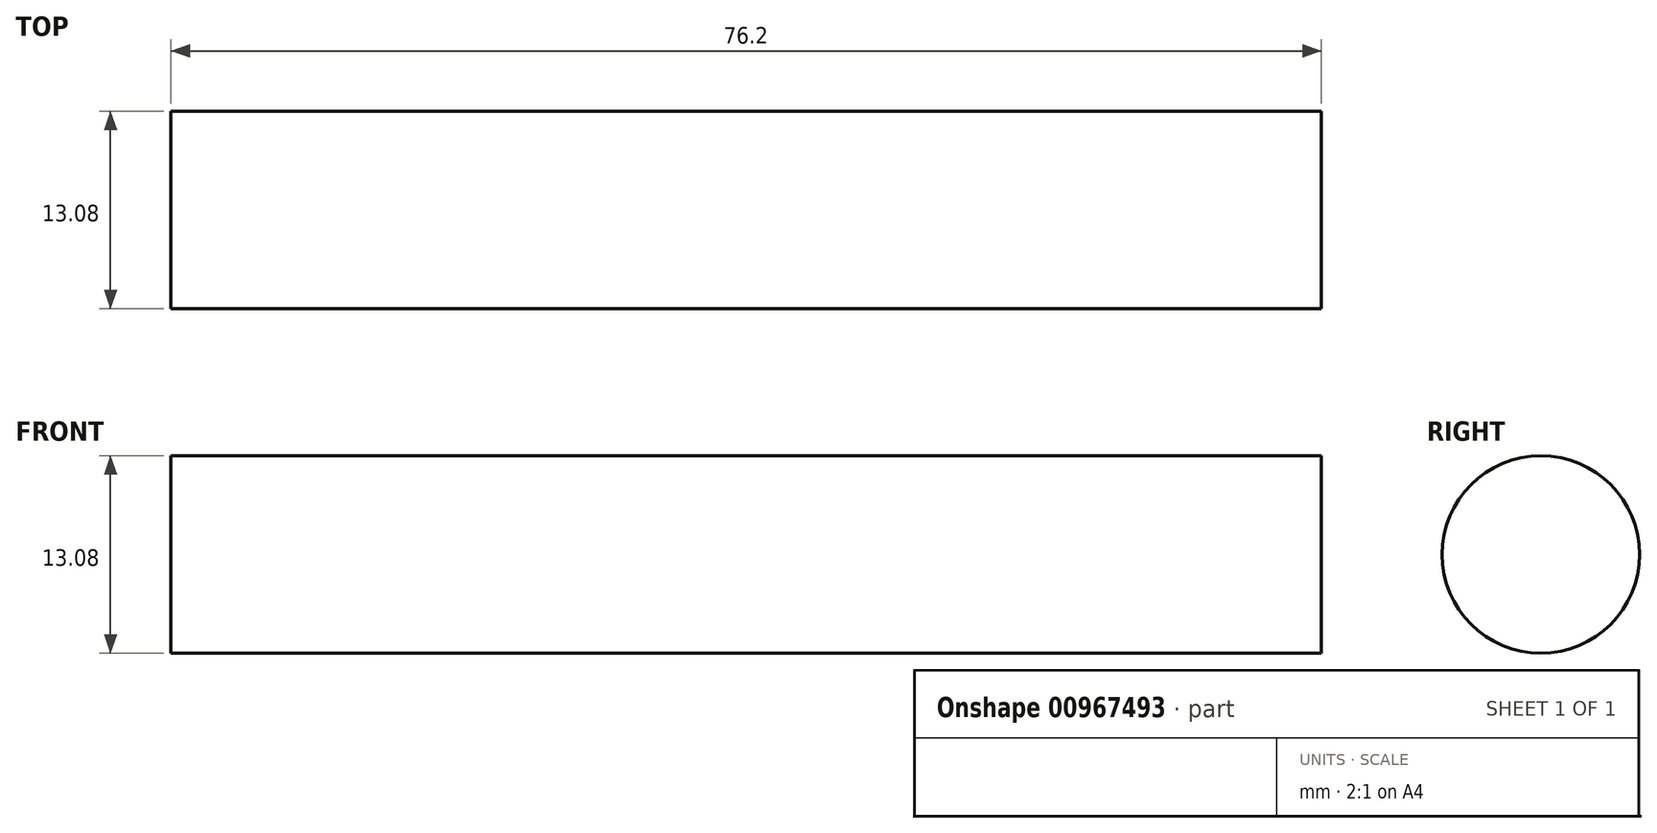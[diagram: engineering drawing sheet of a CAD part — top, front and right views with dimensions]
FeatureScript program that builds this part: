
annotation { "Feature Type Name" : "Feature", "Feature Type Description" : "" }
export const myFeature = defineFeature(function(context is Context, id is Id, definition is map)
    precondition{}
    {
        {
            var Q0;
            Q0=qCreatedBy(makeId("Right.planeOp"),FACE);
            var sketch = newSketch(context, id + "F0", { "sketchPlane" : qUnion([Q0])});
            skCircle(sketch, "E0", {"center": v(0, 0) * mm, "radius": 6.54 * mm});
            skSolve(sketch);
        }
        {
            var Q0;
            Q0=makeQuery(id+"F0.imprint","IMPRINT",FACE,{"disambiguationData":[TD([[makeQuery(id+"F0.imprint","IMPRINT",EDGE,{"derivedFrom":sQuery(id+"F0.wireOp",EDGE,"E0")}),1.0]])]});
            extrude(context, id + "F1", {"entities" : qUnion([Q0]), "depth" : 76.2 * mm, "offsetDistance" : 25.4 * mm});
        }
    });
